# Revit family: HUNTER_WR-CLIK
name_source: partatom
category: Electrical Fixtures
revit_build: Autodesk Revit 2017 (Build: 20190508_0315(x64)
units: mm (PartAtom-declared; Revit-internal decimal feet)

## family parameters
Cut with Voids When Loaded = No
Host = Face
Maintain Annotation Orientation = No
OmniClass Number = 23.27.11.11.23
Part Type = Normal
Room Calculation Point = No
Round Connector Dimension = Use Diameter
Shared = Yes

## types (2) — shared parameters
Assembly Code = G4030100
Default Elevation = 1219 mm
Distance Coverage = 240000 mm  [stored 787.402 ft]
Frequency = 433000000 Hz
Keynote = 32 84 23.05
Manufacturer = Hunter® Industries
Power = 72 VA
Sensor Coverage Zone = Yes
Sensor Height = 76 mm  [stored 0.249344 ft]
Sensor Length = 200 mm  [stored 0.656168 ft]
Sensor Symbol = Yes
Sensor Wiring = Wireless Sensor
Show Antenna = Yes
URL = https://www.hunterindustries.com
Wireless Antenna = Wireless

## per-type parameters (varying)
| type | Description | RAIN-CLIK® Model | Type Comments |
| WR-CLIK | WR-CLIK® Wireless Rain Sensor with built in Quick Response ™ Technology | Wireless Rain Sensor | WR-CLIK® Sensor |
| WRF-CLIK | WRF-CLIK® Wireless Rain / Freeze Sensor with built in Quick Response ™ Technology | Wireless Rain/Freeze-Clik system | WRF-CLIK® Sensor |

note: column(s) folded — value = type name in every type: Model

note: [stored X ft] marks values corroborated as IEEE doubles in the binary element streams (Revit-internal decimal feet)

## geometry (parser evidence)
native form markers: Sweep x10
no freeform markers — native parametric forms only
